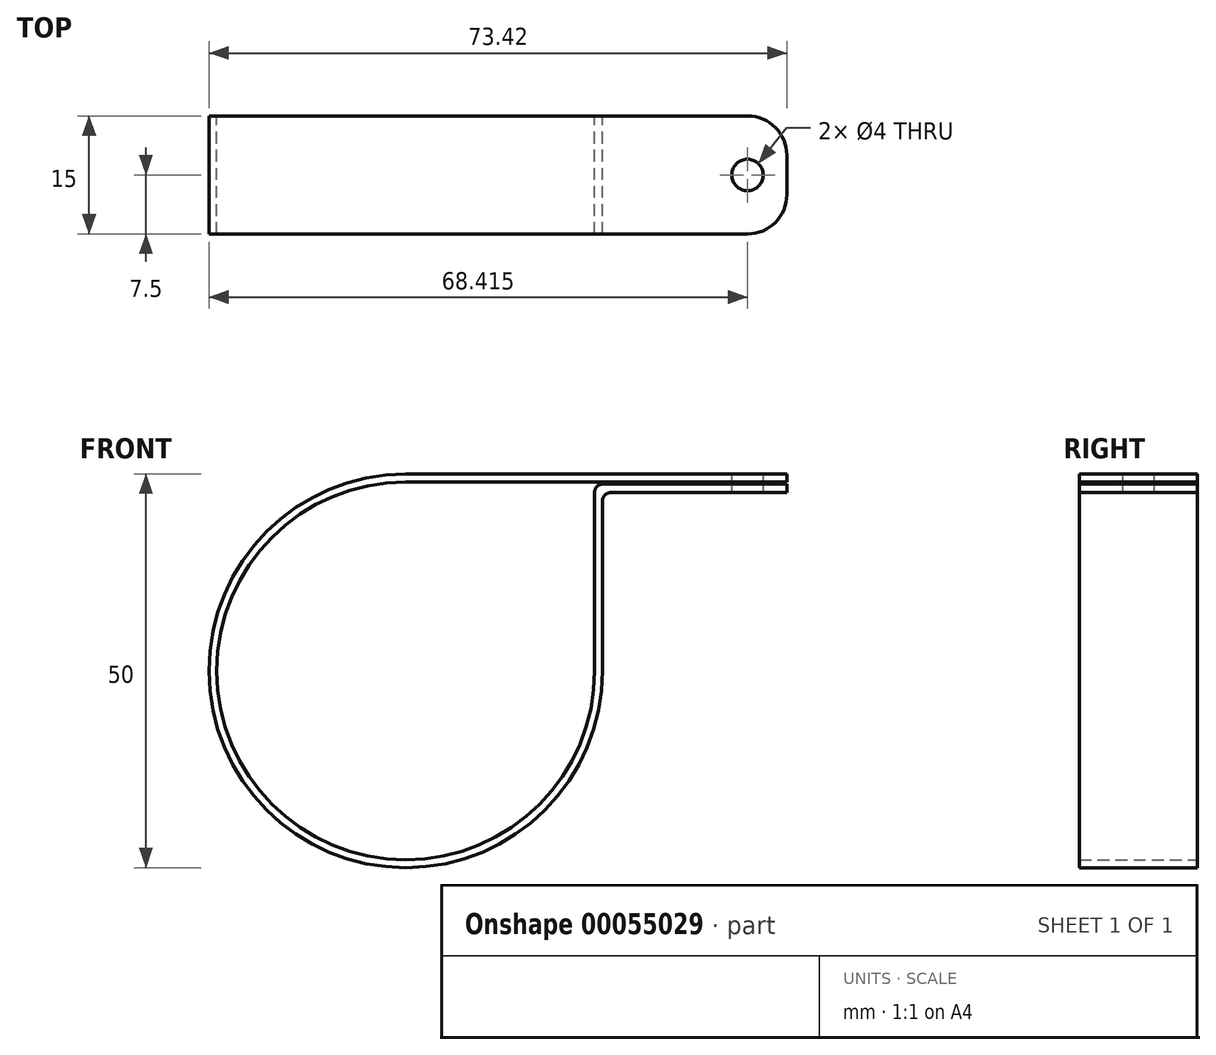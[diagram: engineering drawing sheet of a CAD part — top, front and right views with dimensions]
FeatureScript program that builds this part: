
annotation { "Feature Type Name" : "Feature", "Feature Type Description" : "" }
export const myFeature = defineFeature(function(context is Context, id is Id, definition is map)
    precondition{}
    {
        {
            var Q0;
            Q0=qCreatedBy(makeId("Front.planeOp"),FACE);
            var sketch = newSketch(context, id + "F0", { "sketchPlane" : qUnion([Q0])});
            skArc(sketch, "E0", {"start": v(0, 25) * mm, "mid": v(-17.68, -17.68) * mm, "end": v(25, 0) * mm});
            skArc(sketch, "E1.0", {"start": v(0, 24) * mm, "mid": v(-16.97, -16.97) * mm, "end": v(24, 0) * mm});
            skLineSegment(sketch, "E2", {"start": v(0, 25) * mm, "end": v(48.42, 25) * mm});
            skLineSegment(sketch, "E3", {"start": v(7, 24) * mm, "end": v(48.42, 24) * mm});
            skLineSegment(sketch, "E4", {"start": v(24, 7) * mm, "end": v(24, 22.71) * mm});
            skLineSegment(sketch, "E5", {"start": v(25, 23.71) * mm, "end": v(48.42, 23.71) * mm});
            skLineSegment(sketch, "E6", {"start": v(25, 0) * mm, "end": v(25, 21.63) * mm});
            skLineSegment(sketch, "E7", {"start": v(26, 22.63) * mm, "end": v(48.42, 22.63) * mm});
            skLineSegment(sketch, "E8", {"start": v(48.42, 25) * mm, "end": v(48.42, 24) * mm});
            skLineSegment(sketch, "E9", {"start": v(48.42, 22.63) * mm, "end": v(48.42, 23.71) * mm});
            skPoint(sketch, "E10.orphan", {"position": v(0, 24) * mm});
            skPoint(sketch, "E11.orphan", {"position": v(24, 0) * mm});
            skPoint(sketch, "E12.visualSharp", {"position": v(24, 23.71) * mm});
            skArc(sketch, "E12.filletArc", {"start": v(25, 23.71) * mm, "mid": v(24.3, 23.42) * mm, "end": v(24, 22.71) * mm});
            skPoint(sketch, "E13.visualSharp", {"position": v(25, 22.63) * mm});
            skArc(sketch, "E13.filletArc", {"start": v(26, 22.63) * mm, "mid": v(25.3, 22.34) * mm, "end": v(25, 21.63) * mm});
            skLineSegment(sketch, "E14", {"start": v(0, 24) * mm, "end": v(7, 24) * mm});
            skLineSegment(sketch, "E15", {"start": v(24, 0) * mm, "end": v(24, 7) * mm});
            skSolve(sketch);
        }
        {
            var Q0;
            Q0 = qSketchRegion(id + "F0", true);
            extrude(context, id + "F1", {"entities" : qUnion([Q0]), "depth" : 15 * mm});
        }
        {
            var Q0;
            Q0=makeQuery(id+"F1.opExtrude","SWEPT_FACE",FACE,{"disambiguationData":[OSD([sQuery(id+"F0.wireOp",EDGE,"E2")])]});
            var sketch = newSketch(context, id + "F2", { "sketchPlane" : qUnion([Q0])});
            skLineSegment(sketch, "E16.bottom", {"start": v(43.42, 0) * mm, "end": v(0, 0) * mm});
            skLineSegment(sketch, "E16.top", {"start": v(43.42, -15) * mm, "end": v(0, -15) * mm});
            skLineSegment(sketch, "E16.left", {"start": v(48.42, -5) * mm, "end": v(48.42, -10) * mm});
            skLineSegment(sketch, "E16.right", {"start": v(0, 0) * mm, "end": v(0, -15) * mm});
            skPoint(sketch, "E17.visualSharp", {"position": v(48.42, 0) * mm});
            skArc(sketch, "E17.filletArc", {"start": v(48.42, -5) * mm, "mid": v(46.95, -1.46) * mm, "end": v(43.42, 0) * mm});
            skPoint(sketch, "E18.visualSharp", {"position": v(48.42, -15) * mm});
            skArc(sketch, "E18.filletArc", {"start": v(43.42, -15) * mm, "mid": v(46.95, -13.54) * mm, "end": v(48.42, -10) * mm});
            skLineSegment(sketch, "E19", {"start": v(48.42, -7.5) * mm, "end": v(37.32, -7.5) * mm, "construction": true});
            skLineSegment(sketch, "E20", {"start": v(43.42, 0) * mm, "end": v(43.42, -15.58) * mm, "construction": true});
            skLineSegment(sketch, "E21", {"start": v(43.42, -15.58) * mm, "end": v(43.42, -15) * mm, "construction": true});
            skCircle(sketch, "E22", {"center": v(43.42, -7.5) * mm, "radius": 2 * mm});
            skSolve(sketch);
        }
        {
            var Q0;
            {var subQ0=sQuery(id+"F2.wireOp",EDGE,"E17.filletArc");Q0=makeQuery(id+"F2.imprint","IMPRINT",FACE,{"disambiguationData":[TD([[makeQuery(id+"F2.imprint","IMPRINT",EDGE,{"derivedFrom":subQ0}),-1.0]])]});}
            var Q1;
            {var subQ0=sQuery(id+"F2.wireOp",EDGE,"E18.filletArc");Q1=makeQuery(id+"F2.imprint","IMPRINT",FACE,{"disambiguationData":[TD([[makeQuery(id+"F2.imprint","IMPRINT",EDGE,{"derivedFrom":subQ0}),-1.0]])]});}
            var Q2;
            Q2=makeQuery(id+"F2.imprint","IMPRINT",FACE,{"disambiguationData":[TD([[makeQuery(id+"F2.imprint","IMPRINT",EDGE,{"derivedFrom":sQuery(id+"F2.wireOp",EDGE,"E22")}),1.0]])]});
            extrude(context, id + "F3", {"entities" : qUnion([Q0, Q1, Q2]), "operationType" : NewBodyOperationType.REMOVE, "oppositeDirection" : true, "depth" : 25 * mm});
        }
    });
